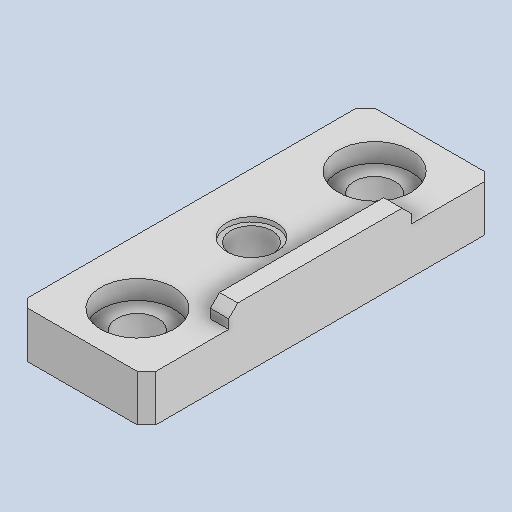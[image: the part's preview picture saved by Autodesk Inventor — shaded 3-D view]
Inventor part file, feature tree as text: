
AUTODESK INVENTOR PART (.ipt)
format: ipt  version: 2024.2 (Build 282272000, 272)  size: 238,080 bytes
history: native  units: in
note: dims shown in document units (in); Inventor stores cm internally (conversion verified against a paired STEP export)
features: extrude x4, chamfer x3, other x2, hole x2, projected_geometry x1
ambient origin geometry x8: Origin, YZ Plane, XZ Plane, XY Plane, X Axis, Y Axis, Z Axis, Center Point
bodies: Solid1 (feature_tree)
feature tree (12):
  other  "Table"
  other  "ADAPTER_RSP05-BH19.05"
  extrude  "Extrusion1"  TaperAngle=0.0deg  [1 undecoded]
  extrude  "Extrusion2"  TaperAngle=0.0deg  [1 undecoded]
  hole  "Hole1"  [1 undecoded]
  chamfer  "Chamfer4"  [1 undecoded]
  extrude  "Extrusion3"  Depth=0.2362in
  hole  "Hole2"  [1 undecoded]
  chamfer  "Chamfer1"  Distance=0.0787in Angle=45.0deg
  chamfer  "Chamfer2"  Distance=0.0787in Angle=45.0deg
  extrude  "Extrusion5"  Depth=0.2165in
  projected_geometry  "Projected Loop1"
note: 5 required parameter values undecoded (feature->parameter linkage not recoverable at this tier; creation-order binding heuristic only, values carry confidence <= 0.55)
